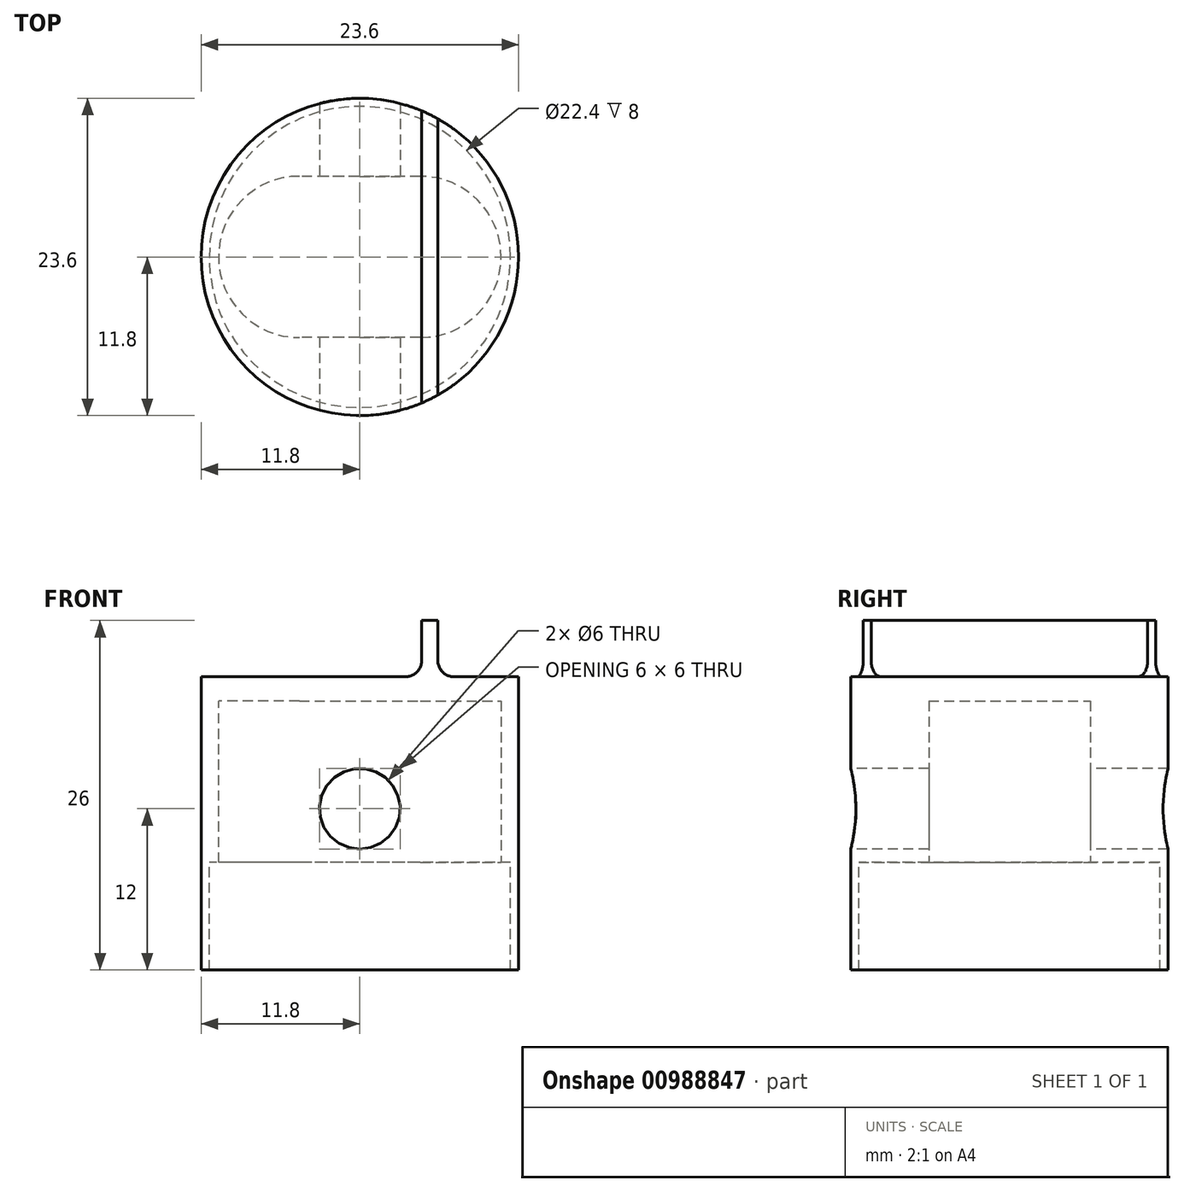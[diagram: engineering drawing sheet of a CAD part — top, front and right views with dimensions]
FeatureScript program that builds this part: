
annotation { "Feature Type Name" : "Feature", "Feature Type Description" : "" }
export const myFeature = defineFeature(function(context is Context, id is Id, definition is map)
    precondition{}
    {
        {
            var Q0;
            Q0=qCreatedBy(makeId("Front.planeOp"),FACE);
            var sketch = newSketch(context, id + "F0", { "sketchPlane" : qUnion([Q0])});
            skLineSegment(sketch, "E0.bottom", {"start": v(0, 0) * mm, "end": v(11.8, 0) * mm});
            skLineSegment(sketch, "E0.top", {"start": v(0, 21.82) * mm, "end": v(11.8, 21.82) * mm});
            skLineSegment(sketch, "E0.left", {"start": v(0, 0) * mm, "end": v(0, 21.82) * mm});
            skLineSegment(sketch, "E0.right", {"start": v(11.8, 0) * mm, "end": v(11.8, 21.82) * mm});
            skSolve(sketch);
        }
        {
            var Q0;
            Q0=makeQuery(id+"F0.imprint","IMPRINT",FACE,{"disambiguationData":[TD([[makeQuery(id+"F0.imprint","IMPRINT",EDGE,{"derivedFrom":sQuery(id+"F0.wireOp",EDGE,"E0.bottom")}),1.0]])]});
            var Q1;
            Q1=sQuery(id+"F0.wireOp",EDGE,"E0.left");
            revolve(context, id + "F1", {"surfaceOperationType" : NewSurfaceOperationType.NEW, "entities" : qUnion([Q0]), "axis" : qUnion([Q1]), "revolveType" : RevolveType.FULL});
        }
        {
            var Q0;
            Q0=qCreatedBy(makeId("Front.planeOp"),FACE);
            var sketch = newSketch(context, id + "F2", { "sketchPlane" : qUnion([Q0])});
            skLineSegment(sketch, "E1.bottom", {"start": v(0, 0) * mm, "end": v(11.2, 0) * mm});
            skLineSegment(sketch, "E1.top", {"start": v(0, 8) * mm, "end": v(11.2, 8) * mm});
            skLineSegment(sketch, "E1.left", {"start": v(0, 0) * mm, "end": v(0, 8) * mm});
            skLineSegment(sketch, "E1.right", {"start": v(11.2, 0) * mm, "end": v(11.2, 8) * mm});
            skSolve(sketch);
        }
        {
            var Q0;
            Q0=qCreatedBy(makeId("Top.planeOp"),FACE);
            var sketch = newSketch(context, id + "F3", { "sketchPlane" : qUnion([Q0])});
            skLineSegment(sketch, "E2.bottom", {"start": v(4.6, -20) * mm, "end": v(5.8, -20) * mm});
            skLineSegment(sketch, "E2.top", {"start": v(4.6, 20) * mm, "end": v(5.8, 20) * mm});
            skLineSegment(sketch, "E2.left", {"start": v(4.6, -20) * mm, "end": v(4.6, 20) * mm});
            skLineSegment(sketch, "E2.right", {"start": v(5.8, -20) * mm, "end": v(5.8, 20) * mm});
            skSolve(sketch);
        }
        {
            var Q0;
            Q0=makeQuery(id+"F3.imprint","IMPRINT",FACE,{"disambiguationData":[TD([[makeQuery(id+"F3.imprint","IMPRINT",EDGE,{"derivedFrom":sQuery(id+"F3.wireOp",EDGE,"E2.bottom")}),1.0]])]});
            extrude(context, id + "F4", {"entities" : qUnion([Q0]), "depth" : 26 * mm, "offsetDistance" : 25 * mm});
        }
        {
            var Q0;
            Q0=qCreatedBy(makeId("Top.planeOp"),FACE);
            var sketch = newSketch(context, id + "F5", { "sketchPlane" : qUnion([Q0])});
            skCircle(sketch, "E3", {"center": v(0, 0) * mm, "radius": 11.8 * mm});
            skSolve(sketch);
        }
        {
            var Q0;
            Q0=makeQuery(id+"F5.imprint","IMPRINT",FACE,{"disambiguationData":[TD([[makeQuery(id+"F5.imprint","IMPRINT",EDGE,{"derivedFrom":sQuery(id+"F5.wireOp",EDGE,"E3")}),1.0]])]});
            extrude(context, id + "F6", {"entities" : qUnion([Q0]), "operationType" : NewBodyOperationType.INTERSECT, "depth" : 30 * mm, "offsetDistance" : 25 * mm});
        }
        {
            var Q0;
            Q0=makeQuery(id+"F4.opExtrude","SWEPT_BODY",BODY,{"disambiguationData":[OSD([sQuery(id+"F3.wireOp",EDGE,"E2.bottom"),sQuery(id+"F3.wireOp",EDGE,"E2.top"),sQuery(id+"F3.wireOp",EDGE,"E2.left"),sQuery(id+"F3.wireOp",EDGE,"E2.right")])]});
            var Q1;
            Q1=makeQuery(id+"F1.opRevolve","SWEPT_BODY",BODY,{"disambiguationData":[OSD([sQuery(id+"F0.wireOp",EDGE,"E0.bottom"),sQuery(id+"F0.wireOp",EDGE,"E0.top"),sQuery(id+"F0.wireOp",EDGE,"E0.left"),sQuery(id+"F0.wireOp",EDGE,"E0.right")])]});
            booleanBodies(context, id + "F7", {"operationType" : BooleanOperationType.UNION, "tools" : qUnion([Q0, Q1])});
        }
        {
            var Q0;
            Q0=makeQuery(id+"F2.imprint","IMPRINT",FACE,{"disambiguationData":[TD([[makeQuery(id+"F2.imprint","IMPRINT",EDGE,{"derivedFrom":sQuery(id+"F2.wireOp",EDGE,"E1.bottom")}),1.0]])]});
            var Q1;
            Q1=sQuery(id+"F2.wireOp",EDGE,"E1.left");
            revolve(context, id + "F8", {"operationType" : NewBodyOperationType.REMOVE, "surfaceOperationType" : NewSurfaceOperationType.NEW, "entities" : qUnion([Q0]), "axis" : qUnion([Q1]), "revolveType" : RevolveType.FULL, "oppositeDirection" : true});
        }
        {
            var Q0;
            Q0=qCreatedBy(makeId("Top.planeOp"),FACE);
            var sketch = newSketch(context, id + "F9", { "sketchPlane" : qUnion([Q0])});
            skLineSegment(sketch, "E4.bottom", {"start": v(-10.5, -6) * mm, "end": v(10.5, -6) * mm});
            skLineSegment(sketch, "E4.top", {"start": v(-10.5, 6) * mm, "end": v(10.5, 6) * mm});
            skLineSegment(sketch, "E4.left", {"start": v(-10.5, -6) * mm, "end": v(-10.5, 6) * mm});
            skLineSegment(sketch, "E4.right", {"start": v(10.5, -6) * mm, "end": v(10.5, 6) * mm});
            skLineSegment(sketch, "E5", {"start": v(-10.5, -6) * mm, "end": v(10.5, 6) * mm, "construction": true});
            skSolve(sketch);
        }
        {
            var Q0;
            Q0=makeQuery(id+"F9.imprint","IMPRINT",FACE,{"disambiguationData":[TD([[makeQuery(id+"F9.imprint","IMPRINT",EDGE,{"derivedFrom":sQuery(id+"F9.wireOp",EDGE,"E4.bottom")}),1.0]])]});
            extrude(context, id + "F10", {"entities" : qUnion([Q0]), "depth" : 20 * mm, "offsetDistance" : 25 * mm});
        }
        {
            var Q0;
            Q0=makeQuery(id+"F10.opExtrude","SWEPT_EDGE",EDGE,{"disambiguationData":[OSD([sQuery(id+"F9.wireOp",EDGE,"E4.bottom"),sQuery(id+"F9.wireOp",EDGE,"E4.left")])]});
            var Q1;
            Q1=makeQuery(id+"F10.opExtrude","SWEPT_EDGE",EDGE,{"disambiguationData":[OSD([sQuery(id+"F9.wireOp",EDGE,"E4.bottom"),sQuery(id+"F9.wireOp",EDGE,"E4.right")])]});
            var Q2;
            Q2=makeQuery(id+"F10.opExtrude","SWEPT_EDGE",EDGE,{"disambiguationData":[OSD([sQuery(id+"F9.wireOp",EDGE,"E4.top"),sQuery(id+"F9.wireOp",EDGE,"E4.left")])]});
            var Q3;
            Q3=makeQuery(id+"F10.opExtrude","SWEPT_EDGE",EDGE,{"disambiguationData":[OSD([sQuery(id+"F9.wireOp",EDGE,"E4.top"),sQuery(id+"F9.wireOp",EDGE,"E4.right")])]});
            fillet(context, id + "F11", {"entities" : qUnion([Q0, Q1, Q2, Q3]), "radius" : 6 * mm, "tangentPropagation" : true, "allowEdgeOverflow" : false});
        }
        {
            var Q0;
            Q0=makeQuery(id+"F10.opExtrude","SWEPT_BODY",BODY,{"disambiguationData":[OSD([sQuery(id+"F9.wireOp",EDGE,"E4.bottom"),sQuery(id+"F9.wireOp",EDGE,"E4.top"),sQuery(id+"F9.wireOp",EDGE,"E4.left"),sQuery(id+"F9.wireOp",EDGE,"E4.right")])]});
            var Q1;
            Q1=makeQuery(id+"F4.opExtrude","SWEPT_BODY",BODY,{"disambiguationData":[OSD([sQuery(id+"F3.wireOp",EDGE,"E2.bottom"),sQuery(id+"F3.wireOp",EDGE,"E2.top"),sQuery(id+"F3.wireOp",EDGE,"E2.left"),sQuery(id+"F3.wireOp",EDGE,"E2.right")])]});
            booleanBodies(context, id + "F12", {"operationType" : BooleanOperationType.SUBTRACTION, "tools" : qUnion([Q0]), "targets" : qUnion([Q1])});
        }
        {
            var Q0;
            Q0=makeQuery(id+"F7.opBoolean","INTERSECT",EDGE,{"derivedFrom":[makeQuery(id+"F1.opRevolve","SWEPT_FACE",FACE,{"disambiguationData":[OSD([sQuery(id+"F0.wireOp",EDGE,"E0.top")])]}),makeQuery(id+"F4.opExtrude","SWEPT_FACE",FACE,{"disambiguationData":[OSD([sQuery(id+"F3.wireOp",EDGE,"E2.left")])]})]});
            var Q1;
            Q1=makeQuery(id+"F7.opBoolean","INTERSECT",EDGE,{"derivedFrom":[makeQuery(id+"F1.opRevolve","SWEPT_FACE",FACE,{"disambiguationData":[OSD([sQuery(id+"F0.wireOp",EDGE,"E0.top")])]}),makeQuery(id+"F4.opExtrude","SWEPT_FACE",FACE,{"disambiguationData":[OSD([sQuery(id+"F3.wireOp",EDGE,"E2.right")])]})]});
            fillet(context, id + "F13", {"entities" : qUnion([Q0, Q1]), "radius" : 1.2 * mm, "tangentPropagation" : true, "allowEdgeOverflow" : false});
        }
        {
            var Q0;
            Q0=qCreatedBy(makeId("Front.planeOp"),FACE);
            var sketch = newSketch(context, id + "F14", { "sketchPlane" : qUnion([Q0])});
            skCircle(sketch, "E6", {"center": v(0, 12) * mm, "radius": 3 * mm});
            skSolve(sketch);
        }
        {
            var Q0;
            Q0 = qSketchRegion(id + "F14", true);
            extrude(context, id + "F15", {"entities" : qUnion([Q0]), "operationType" : NewBodyOperationType.REMOVE, "oppositeDirection" : true, "depth" : 25 * mm, "offsetDistance" : 25 * mm, "symmetric" : true});
        }
    });
